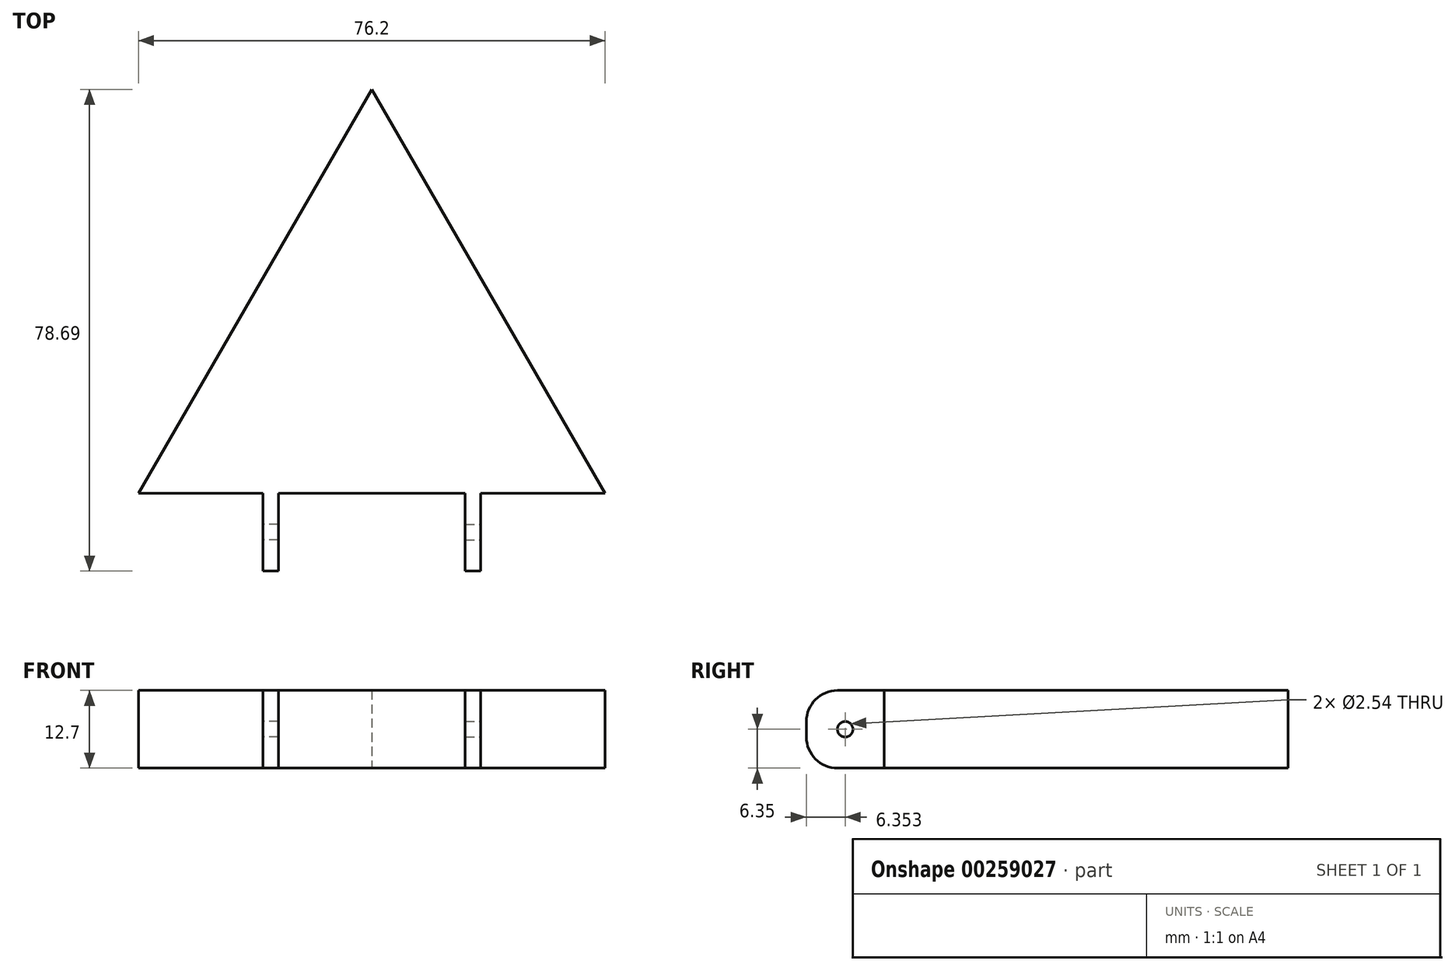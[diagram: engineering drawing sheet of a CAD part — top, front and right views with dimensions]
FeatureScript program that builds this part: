
annotation { "Feature Type Name" : "Feature", "Feature Type Description" : "" }
export const myFeature = defineFeature(function(context is Context, id is Id, definition is map)
    precondition{}
    {
        {
            var Q0;
            Q0=qCreatedBy(makeId("Top.planeOp"),FACE);
            var sketch = newSketch(context, id + "F0", { "sketchPlane" : qUnion([Q0])});
            skCircle(sketch, "E0.cCircle", {"center": v(0, 0) * mm, "radius": 22 * mm, "construction": true});
            skLineSegment(sketch, "E0.0", {"start": v(38.1, -22) * mm, "end": v(-38.1, -22) * mm});
            skLineSegment(sketch, "E0.1", {"start": v(-38.1, -22) * mm, "end": v(0, 44) * mm});
            skLineSegment(sketch, "E0.2", {"start": v(0, 44) * mm, "end": v(38.1, -22) * mm});
            skPoint(sketch, "E0.0.midPoint", {"position": v(0, -22) * mm});
            skSolve(sketch);
        }
        {
            var Q0;
            Q0=makeQuery(id+"F0.imprint","IMPRINT",FACE,{"disambiguationData":[TD([[makeQuery(id+"F0.imprint","IMPRINT",EDGE,{"derivedFrom":sQuery(id+"F0.wireOp",EDGE,"E0.0")}),-1.0]])]});
            extrude(context, id + "F1", {"entities" : qUnion([Q0]), "depth" : 12.7 * mm});
        }
        {
            var Q0;
            Q0=makeQuery(id+"F1.opExtrude","SWEPT_FACE",FACE,{"disambiguationData":[OSD([sQuery(id+"F0.wireOp",EDGE,"E0.0")])]});
            var sketch = newSketch(context, id + "F2", { "sketchPlane" : qUnion([Q0])});
            skLineSegment(sketch, "E1", {"start": v(0, 12.7) * mm, "end": v(15.24, 12.7) * mm, "construction": true});
            skLineSegment(sketch, "E2", {"start": v(0, 12.7) * mm, "end": v(-15.24, 12.7) * mm, "construction": true});
            skLineSegment(sketch, "E3.bottom", {"start": v(-15.24, 12.7) * mm, "end": v(-17.78, 12.7) * mm});
            skLineSegment(sketch, "E3.top", {"start": v(-15.24, 0) * mm, "end": v(-17.78, 0) * mm});
            skLineSegment(sketch, "E3.left", {"start": v(-15.24, 12.7) * mm, "end": v(-15.24, 0) * mm});
            skLineSegment(sketch, "E3.right", {"start": v(-17.78, 12.7) * mm, "end": v(-17.78, 0) * mm});
            skLineSegment(sketch, "E4.bottom", {"start": v(15.24, 12.7) * mm, "end": v(17.78, 12.7) * mm});
            skLineSegment(sketch, "E4.top", {"start": v(15.24, 0) * mm, "end": v(17.78, 0) * mm});
            skLineSegment(sketch, "E4.left", {"start": v(15.24, 12.7) * mm, "end": v(15.24, 0) * mm});
            skLineSegment(sketch, "E4.right", {"start": v(17.78, 12.7) * mm, "end": v(17.78, 0) * mm});
            skSolve(sketch);
        }
        {
            var Q0;
            Q0=makeQuery(id+"F2.imprint","IMPRINT",FACE,{"disambiguationData":[TD([[makeQuery(id+"F2.imprint","IMPRINT",EDGE,{"derivedFrom":sQuery(id+"F2.wireOp",EDGE,"E3.bottom")}),1.0]])]});
            var Q1;
            Q1=makeQuery(id+"F2.imprint","IMPRINT",FACE,{"disambiguationData":[TD([[makeQuery(id+"F2.imprint","IMPRINT",EDGE,{"derivedFrom":sQuery(id+"F2.wireOp",EDGE,"E4.bottom")}),1.0]])]});
            extrude(context, id + "F3", {"entities" : qUnion([Q0, Q1]), "operationType" : NewBodyOperationType.ADD, "depth" : 12.7 * mm});
        }
        {
            var Q0;
            Q0=makeQuery(id+"F3.opExtrude","SWEPT_FACE",FACE,{"disambiguationData":[OSD([sQuery(id+"F2.wireOp",EDGE,"E4.right")])]});
            var sketch = newSketch(context, id + "F4", { "sketchPlane" : qUnion([Q0])});
            skLineSegment(sketch, "E5", {"start": v(-34.7, 12.7) * mm, "end": v(-22, 0) * mm, "construction": true});
            skLineSegment(sketch, "E6", {"start": v(-22, 12.7) * mm, "end": v(-34.7, 0) * mm, "construction": true});
            skCircle(sketch, "E7", {"center": v(-28.35, 6.35) * mm, "radius": 1.27 * mm});
            skSolve(sketch);
        }
        {
            var Q0;
            Q0=makeQuery(id+"F4.imprint","IMPRINT",FACE,{"disambiguationData":[TD([[makeQuery(id+"F4.imprint","IMPRINT",EDGE,{"derivedFrom":sQuery(id+"F4.wireOp",EDGE,"E7")}),1.0]])]});
            extrude(context, id + "F5", {"entities" : qUnion([Q0]), "operationType" : NewBodyOperationType.REMOVE, "oppositeDirection" : true, "depth" : 25.4 * mm});
        }
        {
            var Q0;
            Q0=makeQuery(id+"F3.opExtrude","SWEPT_FACE",FACE,{"disambiguationData":[OSD([sQuery(id+"F2.wireOp",EDGE,"E3.right")])]});
            var sketch = newSketch(context, id + "F6", { "sketchPlane" : qUnion([Q0])});
            skLineSegment(sketch, "E8", {"start": v(22, 12.7) * mm, "end": v(34.7, 0) * mm, "construction": true});
            skLineSegment(sketch, "E9", {"start": v(34.7, 12.7) * mm, "end": v(22, 0) * mm, "construction": true});
            skCircle(sketch, "E10", {"center": v(28.35, 6.35) * mm, "radius": 1.27 * mm});
            skSolve(sketch);
        }
        {
            var Q0;
            Q0=makeQuery(id+"F6.imprint","IMPRINT",FACE,{"disambiguationData":[TD([[makeQuery(id+"F6.imprint","IMPRINT",EDGE,{"derivedFrom":sQuery(id+"F6.wireOp",EDGE,"E10")}),1.0]])]});
            extrude(context, id + "F7", {"entities" : qUnion([Q0]), "operationType" : NewBodyOperationType.REMOVE, "oppositeDirection" : true, "depth" : 25.4 * mm});
        }
        {
            var Q0;
            Q0=makeQuery(id+"F3.opExtrude","CAP_EDGE",EDGE,{"disambiguationData":[OSD([sQuery(id+"F2.wireOp",EDGE,"E3.bottom")])],"isStart":false});
            var Q1;
            Q1=makeQuery(id+"F3.opExtrude","CAP_EDGE",EDGE,{"disambiguationData":[OSD([sQuery(id+"F2.wireOp",EDGE,"E3.top")])],"isStart":false});
            var Q2;
            Q2=makeQuery(id+"F3.opExtrude","CAP_EDGE",EDGE,{"disambiguationData":[OSD([sQuery(id+"F2.wireOp",EDGE,"E4.top")])],"isStart":false});
            var Q3;
            Q3=makeQuery(id+"F3.opExtrude","CAP_EDGE",EDGE,{"disambiguationData":[OSD([sQuery(id+"F2.wireOp",EDGE,"E4.bottom")])],"isStart":false});
            fillet(context, id + "F8", {"entities" : qUnion([Q0, Q1, Q2, Q3]), "radius" : 5.08 * mm, "tangentPropagation" : true, "allowEdgeOverflow" : false});
        }
    });
